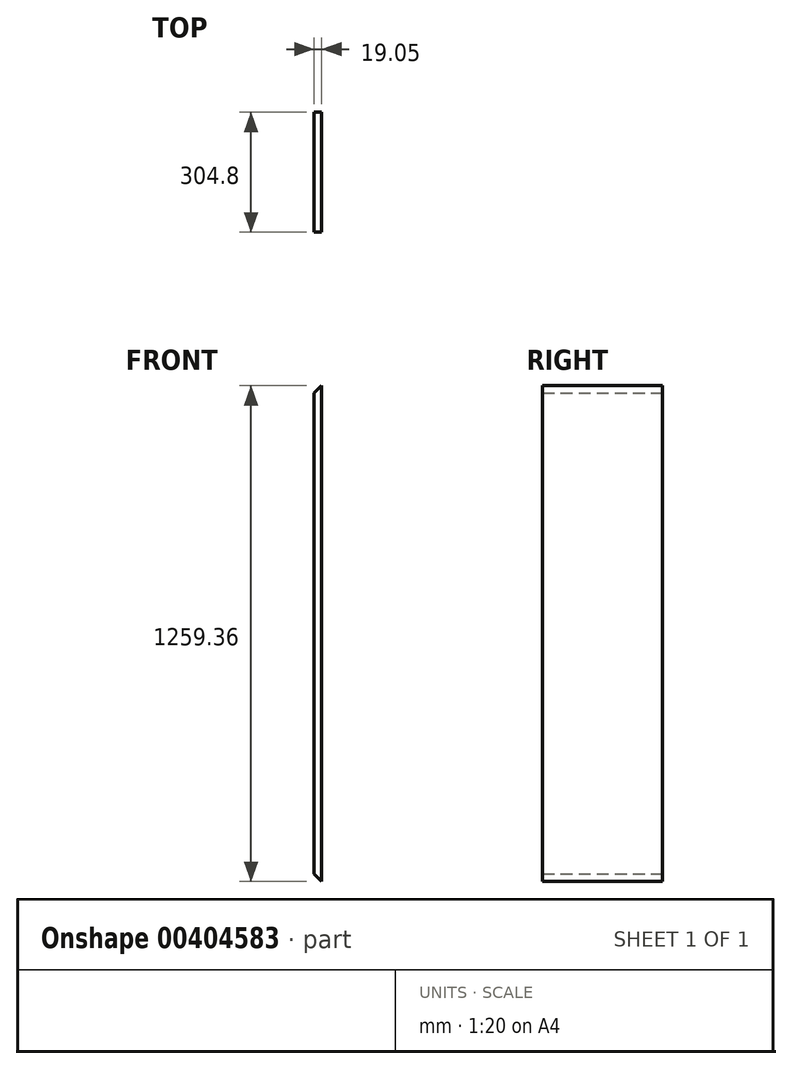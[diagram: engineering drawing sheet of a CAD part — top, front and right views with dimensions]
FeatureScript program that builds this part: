
annotation { "Feature Type Name" : "Feature", "Feature Type Description" : "" }
export const myFeature = defineFeature(function(context is Context, id is Id, definition is map)
    precondition{}
    {
        {
            var Q0;
            Q0=qCreatedBy(makeId("Front.planeOp"),FACE);
            var sketch = newSketch(context, id + "F0", { "sketchPlane" : qUnion([Q0])});
            skLineSegment(sketch, "E0.right", {"start": v(19.05, -610.63) * mm, "end": v(19.05, 610.63) * mm});
            skLineSegment(sketch, "E1.MirrorCS", {"start": v(38.1, -629.68) * mm, "end": v(38.1, 629.68) * mm});
            skLineSegment(sketch, "E2.MirrorCS", {"start": v(38.1, -629.68) * mm, "end": v(19.05, -610.63) * mm});
            skLineSegment(sketch, "E3.MirrorCS", {"start": v(38.1, 629.68) * mm, "end": v(19.05, 610.63) * mm});
            skSolve(sketch);
        }
        {
            var Q0;
            Q0 = qSketchRegion(id + "F0", true);
            extrude(context, id + "F1", {"entities" : qUnion([Q0]), "endBound" : BoundingType.SYMMETRIC, "depth" : 304.8 * mm});
        }
    });
